# Revit family: 1122A_LightHAWK2_Dimming
name_source: partatom
category: Communication Devices
units: mm (PartAtom-declared; Revit-internal decimal feet)

## family parameters
Cut with Voids When Loaded = No
Host = Face
Maintain Annotation Orientation = No
OmniClass Number = 23.85.80.11.27
OmniClass Title = Lighting Controls
Part Type = Normal
Room Calculation Point = No
Round Connector Dimension = Use Diameter
Shared = Yes

## types (1)
- 1122A_LightHAWK2_Dimming
    Assembly Code = D5090
    Black = Paint -Carbon Black
    Default Elevation = 48 "
    Description = The LightHAWK2 Passive Infrared Wall Switch Sensor uses passive
infrared (PIR) technology to detect motion. The most affordable of the
motion detecting technologies, this sensor type is ideal for detecting
large motion in areas with an unobstructed view of the sensor. This
sensor has a coverage area of up to 1,000 square feet and 180° of
detection.
    Features = Digital passive infrared (PIR) sensor 
IntelliDAPT self-adaptive technology—no manual adjustment required 
1 relay model for single-level switching 
Occupancy (auto-on) and Vacancy (manual-on) operating modes
1,000 square-foot, 180° coverage area  
RhinoTuff™ vandal resistant lens 
120/277VAC operation
No minimum load requirement 
 Zero Arc Point Switching
Five-year warranty 
120-277 Vac and 347 Vac models
    Height = 4.5 "
    Manufacturer = NX Lighting Controls
    Model = Wall Switch Occupancy Sensors
    Type Comments = LightHAWK®2 Dimming Wall Switch Sensor
    URL = https://www.currentlighting.com
    Warranty = 5-Years Warranty
    White = Paint - Matte White
    Width = 2.75 "

## geometry (parser evidence)
native form markers: Sweep x2
no freeform markers — native parametric forms only
